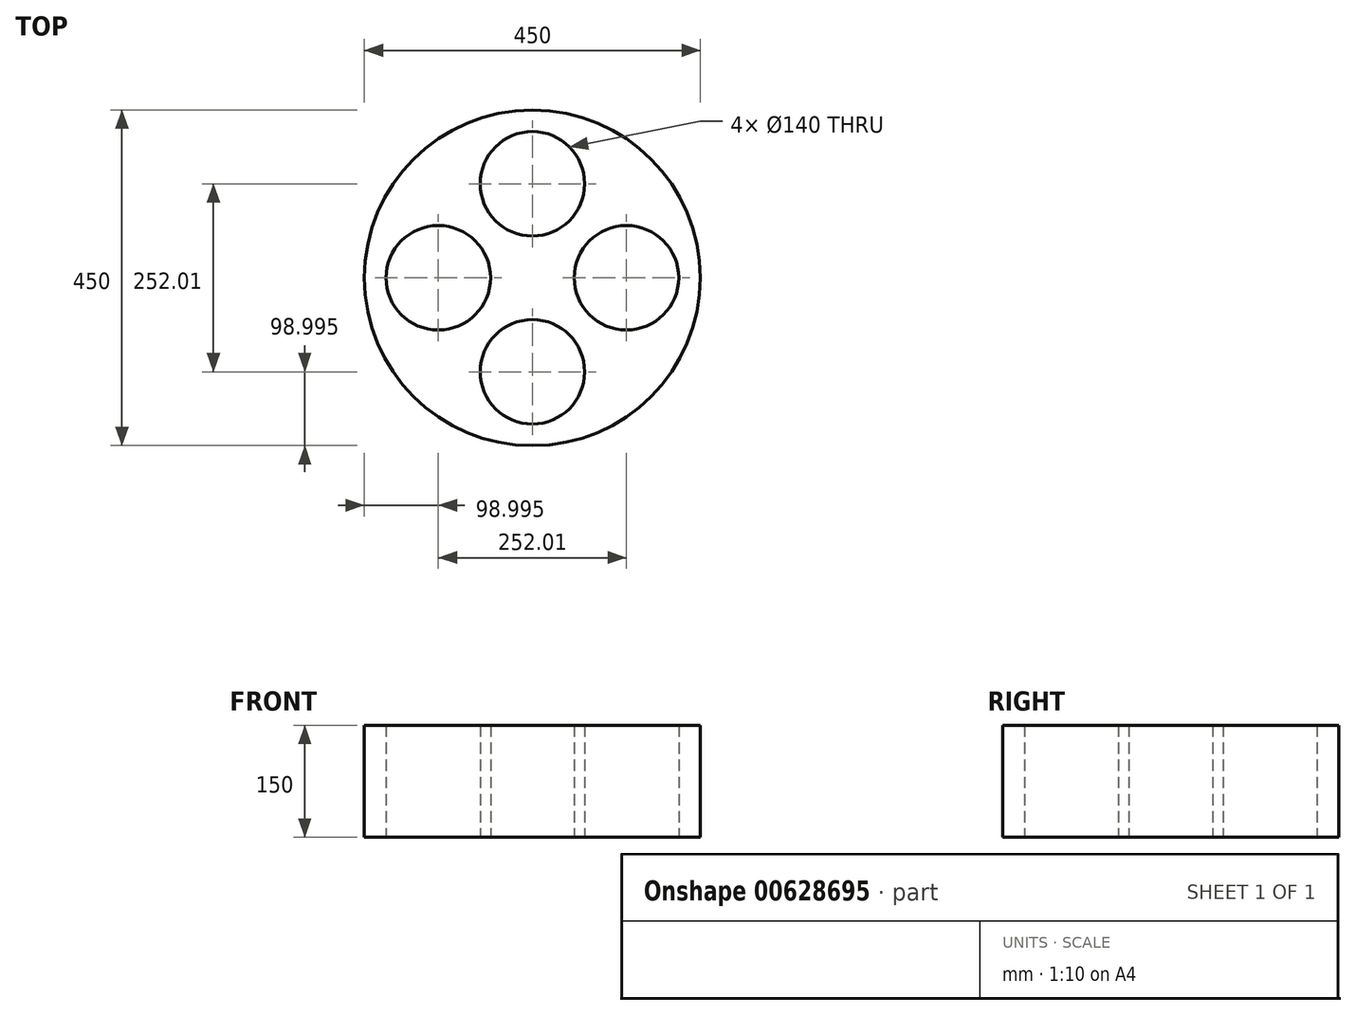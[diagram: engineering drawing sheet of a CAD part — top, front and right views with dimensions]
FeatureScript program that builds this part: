
annotation { "Feature Type Name" : "Feature", "Feature Type Description" : "" }
export const myFeature = defineFeature(function(context is Context, id is Id, definition is map)
    precondition{}
    {
        {
            var Q0;
            Q0=qCreatedBy(makeId("Top.planeOp"),FACE);
            var sketch = newSketch(context, id + "F0", { "sketchPlane" : qUnion([Q0])});
            skCircle(sketch, "E0", {"center": v(0, 0) * mm, "radius": 225 * mm});
            skLineSegment(sketch, "E1", {"start": v(0, 0) * mm, "end": v(0, 225) * mm, "construction": true});
            skLineSegment(sketch, "E2", {"start": v(0, 225) * mm, "end": v(0, -225) * mm, "construction": true});
            skLineSegment(sketch, "E3", {"start": v(0, -225) * mm, "end": v(-225, 0) * mm, "construction": true});
            skLineSegment(sketch, "E4", {"start": v(-225, 0) * mm, "end": v(0, 225) * mm, "construction": true});
            skLineSegment(sketch, "E5", {"start": v(0, 225) * mm, "end": v(225, 0) * mm, "construction": true});
            skLineSegment(sketch, "E6", {"start": v(225, 0) * mm, "end": v(0, -225) * mm, "construction": true});
            skCircle(sketch, "E7", {"center": v(0, 126) * mm, "radius": 70 * mm});
            skCircle(sketch, "E8.1.0", {"center": v(-126, 0) * mm, "radius": 70 * mm});
            skCircle(sketch, "E8.2.0", {"center": v(0, -126) * mm, "radius": 70 * mm});
            skCircle(sketch, "E8.3.0", {"center": v(126, 0) * mm, "radius": 70 * mm});
            skLineSegment(sketch, "E9", {"start": v(-225, 0) * mm, "end": v(225, 0) * mm, "construction": true});
            skSolve(sketch);
        }
        {
            var Q0;
            Q0=makeQuery(id+"F0.imprint","IMPRINT",FACE,{"disambiguationData":[TD([[makeQuery(id+"F0.imprint","IMPRINT",EDGE,{"derivedFrom":sQuery(id+"F0.wireOp",EDGE,"E0")}),1.0]])]});
            extrude(context, id + "F1", {"entities" : qUnion([Q0]), "depth" : 150 * mm, "offsetDistance" : 25 * mm});
        }
    });
